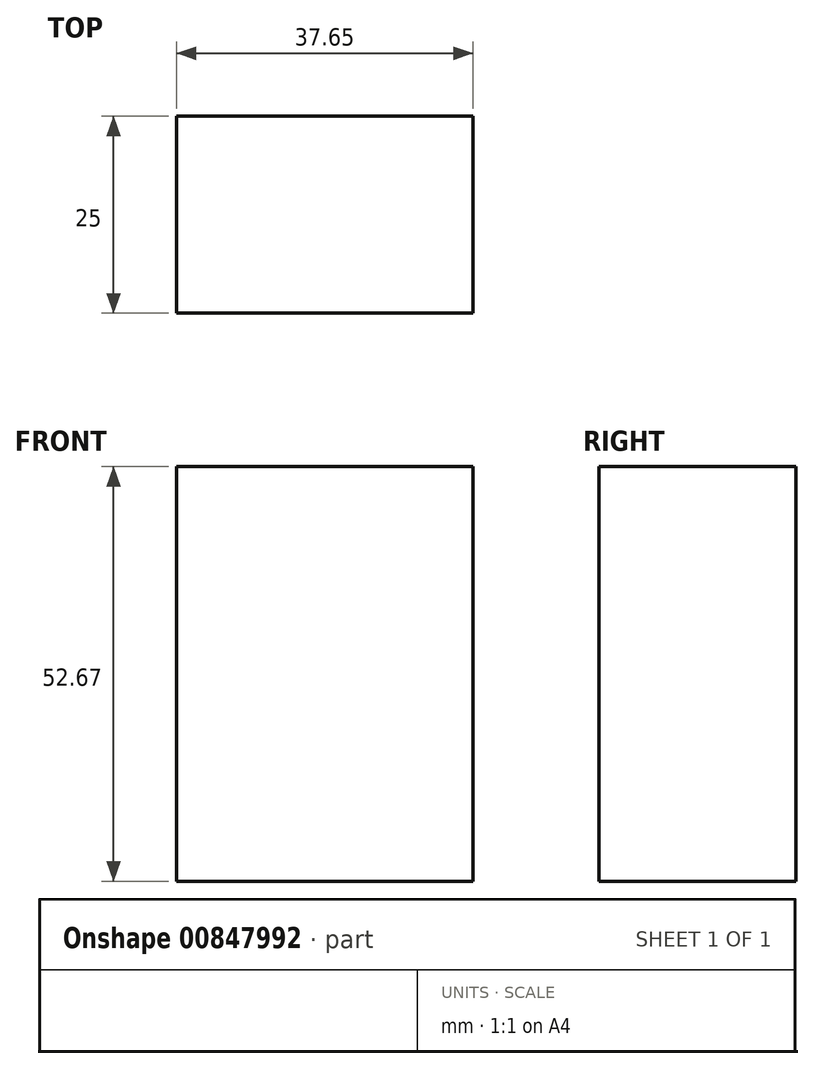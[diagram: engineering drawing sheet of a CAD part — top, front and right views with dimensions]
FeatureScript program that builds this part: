
annotation { "Feature Type Name" : "Feature", "Feature Type Description" : "" }
export const myFeature = defineFeature(function(context is Context, id is Id, definition is map)
    precondition{}
    {
        {
            var Q0;
            Q0=qCreatedBy(makeId("Front.planeOp"),FACE);
            var sketch = newSketch(context, id + "F0", { "sketchPlane" : qUnion([Q0])});
            skLineSegment(sketch, "E0.bottom", {"start": v(-139.51, 45.96) * mm, "end": v(-101.86, 45.96) * mm});
            skLineSegment(sketch, "E0.top", {"start": v(-139.51, -6.71) * mm, "end": v(-101.86, -6.71) * mm});
            skLineSegment(sketch, "E0.left", {"start": v(-139.51, 45.96) * mm, "end": v(-139.51, -6.71) * mm});
            skLineSegment(sketch, "E0.right", {"start": v(-101.86, 45.96) * mm, "end": v(-101.86, -6.71) * mm});
            skSolve(sketch);
        }
        {
            var Q0;
            Q0 = qSketchRegion(id + "F0", true);
            extrude(context, id + "F1", {"entities" : qUnion([Q0]), "depth" : 25 * mm, "offsetDistance" : 25 * mm});
        }
    });
